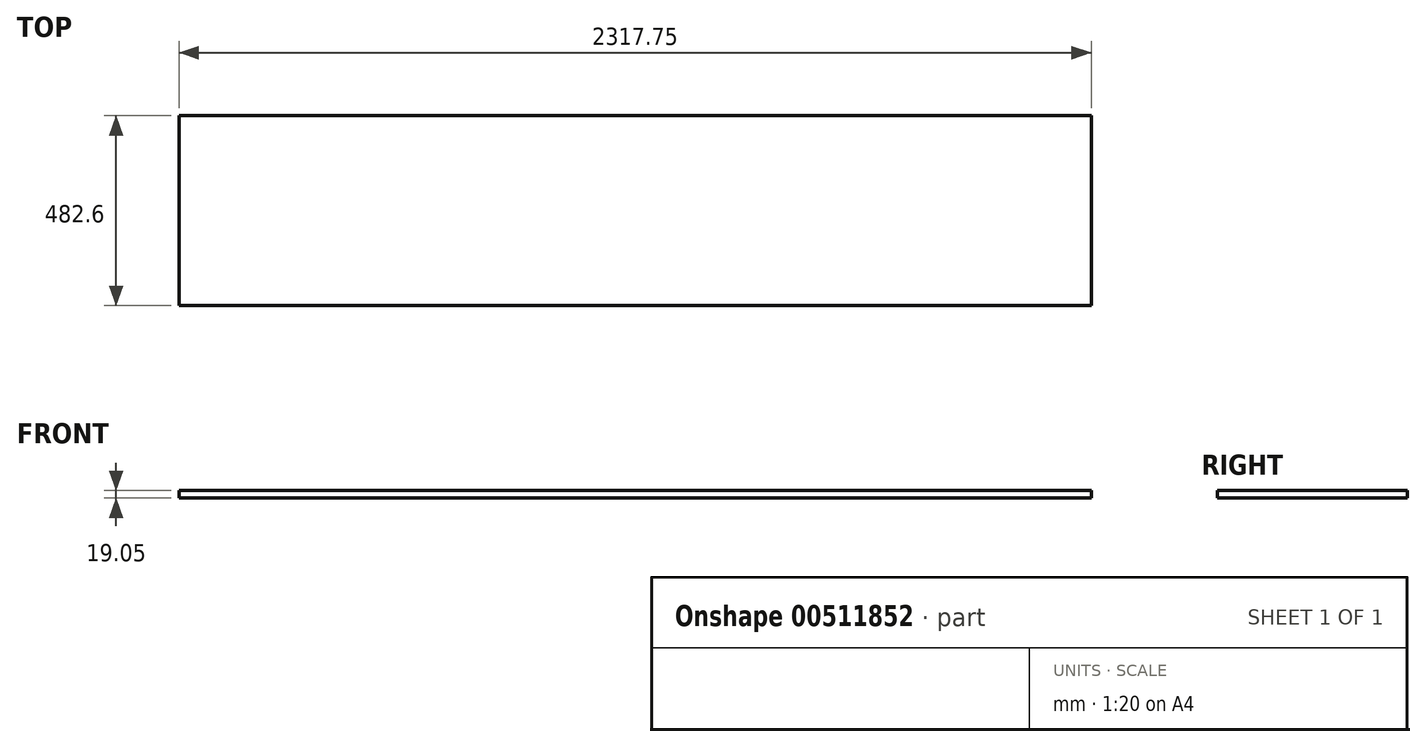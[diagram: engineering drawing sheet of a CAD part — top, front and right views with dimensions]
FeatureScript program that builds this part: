
annotation { "Feature Type Name" : "Feature", "Feature Type Description" : "" }
export const myFeature = defineFeature(function(context is Context, id is Id, definition is map)
    precondition{}
    {
        {
            var Q0;
            Q0=qCreatedBy(makeId("Top.planeOp"),FACE);
            var sketch = newSketch(context, id + "F0", { "sketchPlane" : qUnion([Q0])});
            skLineSegment(sketch, "E0.bottom", {"start": v(-1150.1, 312.82) * mm, "end": v(1167.65, 312.82) * mm});
            skLineSegment(sketch, "E0.top", {"start": v(-1150.1, -169.78) * mm, "end": v(1167.65, -169.78) * mm});
            skLineSegment(sketch, "E0.left", {"start": v(-1150.1, 312.82) * mm, "end": v(-1150.1, -169.78) * mm});
            skLineSegment(sketch, "E0.right", {"start": v(1167.65, 312.82) * mm, "end": v(1167.65, -169.78) * mm});
            skSolve(sketch);
        }
        {
            var Q0;
            Q0=makeQuery(id+"F0.imprint","IMPRINT",FACE,{"disambiguationData":[TD([[makeQuery(id+"F0.imprint","IMPRINT",EDGE,{"derivedFrom":sQuery(id+"F0.wireOp",EDGE,"E0.bottom")}),-1.0]])]});
            extrude(context, id + "F1", {"entities" : qUnion([Q0]), "depth" : 19.05 * mm});
        }
    });
